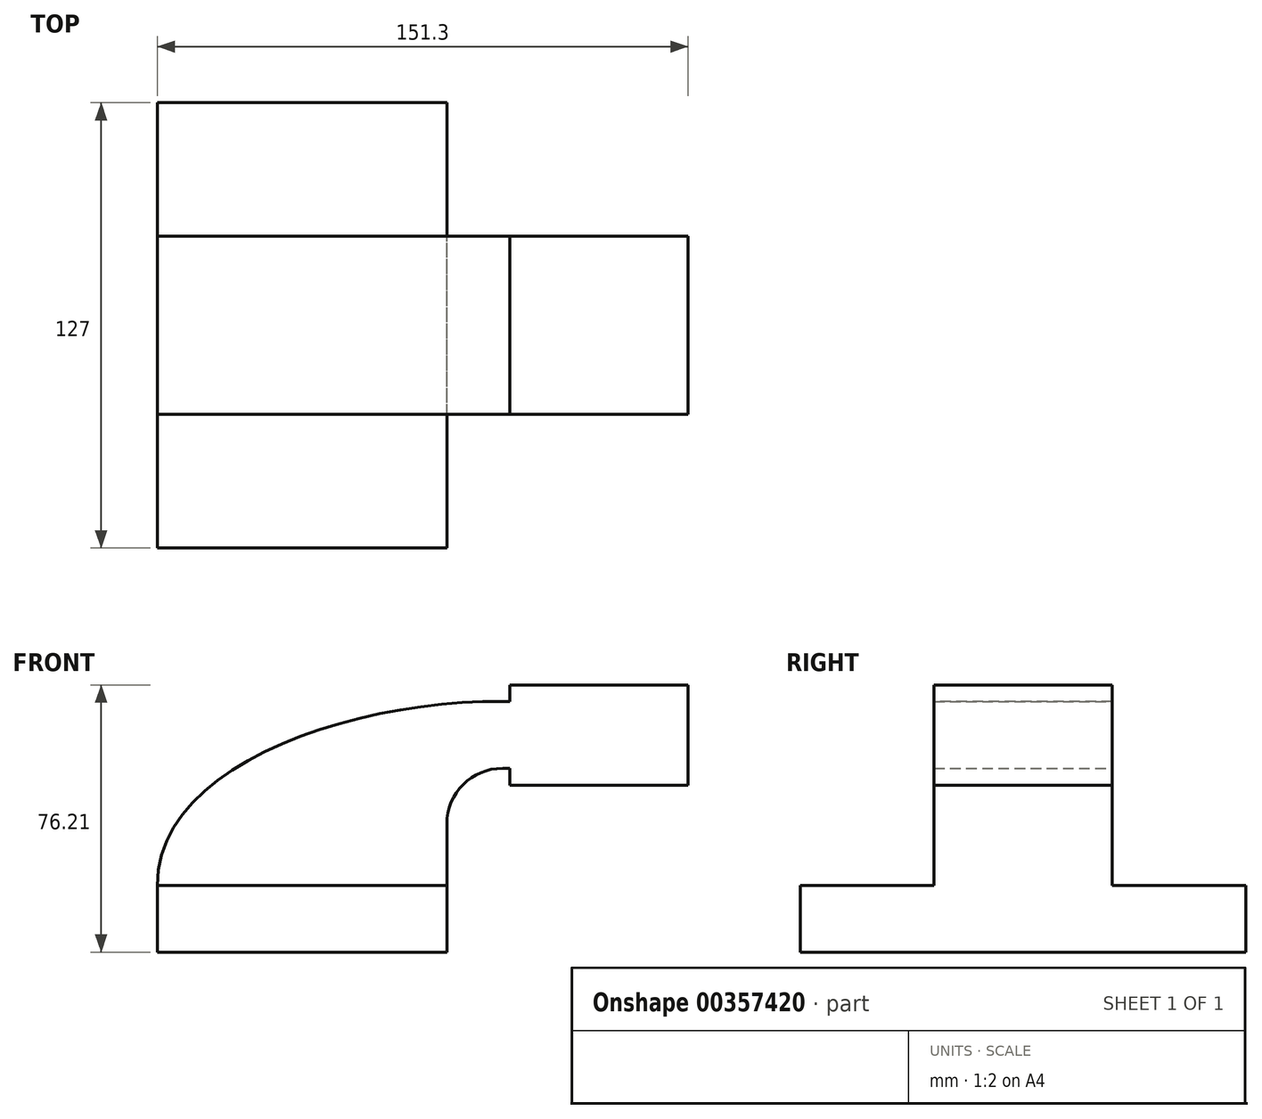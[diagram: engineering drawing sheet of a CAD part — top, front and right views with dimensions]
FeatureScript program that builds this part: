
annotation { "Feature Type Name" : "Feature", "Feature Type Description" : "" }
export const myFeature = defineFeature(function(context is Context, id is Id, definition is map)
    precondition{}
    {
        {
            var Q0;
            Q0=qCreatedBy(makeId("Front.planeOp"),FACE);
            var sketch = newSketch(context, id + "F0", { "sketchPlane" : qUnion([Q0])});
            skLineSegment(sketch, "E0.bottom", {"start": v(-41.28, -9.53) * mm, "end": v(41.28, -9.53) * mm});
            skLineSegment(sketch, "E0.top", {"start": v(-41.28, 9.53) * mm, "end": v(41.28, 9.53) * mm});
            skLineSegment(sketch, "E0.left", {"start": v(-41.27, -9.53) * mm, "end": v(-41.28, 9.53) * mm});
            skLineSegment(sketch, "E0.right", {"start": v(41.28, -9.53) * mm, "end": v(41.28, 9.53) * mm});
            skPoint(sketch, "E0.middle", {"position": v(0, 0) * mm});
            skLineSegment(sketch, "E1.bottom", {"start": v(59.22, 38.1) * mm, "end": v(110.02, 38.1) * mm});
            skLineSegment(sketch, "E1.top", {"start": v(59.22, 66.67) * mm, "end": v(110.02, 66.67) * mm});
            skLineSegment(sketch, "E1.left", {"start": v(59.22, 38.1) * mm, "end": v(59.22, 66.67) * mm});
            skLineSegment(sketch, "E1.right", {"start": v(110.02, 38.1) * mm, "end": v(110.02, 66.67) * mm});
            skPoint(sketch, "E1.middle", {"position": v(84.62, 52.39) * mm});
            skLineSegment(sketch, "E2", {"start": v(41.27, 9.53) * mm, "end": v(41.27, 27) * mm});
            skArc(sketch, "E3", {"start": v(41.27, 27) * mm, "mid": v(45.92, 38.23) * mm, "end": v(57.15, 42.88) * mm});
            skLineSegment(sketch, "E4", {"start": v(57.15, 42.88) * mm, "end": v(85.72, 42.88) * mm});
            skLineSegment(sketch, "E5.0", {"start": v(57.15, 61.93) * mm, "end": v(84.62, 61.93) * mm});
            skArc(sketch, "E5.1", {"start": v(22.22, 27) * mm, "mid": v(32.45, 51.7) * mm, "end": v(57.15, 61.93) * mm});
            skLineSegment(sketch, "E5.2", {"start": v(22.22, 9.53) * mm, "end": v(22.22, 27) * mm});
            skLineSegment(sketch, "E6", {"start": v(84.62, 38.1) * mm, "end": v(84.62, 66.68) * mm});
            skFitSpline(sketch, "E7", {"points": [v(-41.28, 9.53) * mm, v(57.15, 61.93) * mm], "startDerivative": vector(0.05, 102.9) * mm, "endDerivative": vector(129.47, -1.26) * mm});
            skSolve(sketch);
        }
        {
            var Q0;
            Q0=makeQuery(id+"F0.imprint","IMPRINT",FACE,{"disambiguationData":[TD([[makeQuery(id+"F0.imprint","IMPRINT",EDGE,{"derivedFrom":sQuery(id+"F0.wireOp",EDGE,"E0.bottom")}),1.0]])]});
            extrude(context, id + "F1", {"entities" : qUnion([Q0]), "endBound" : BoundingType.SYMMETRIC, "depth" : 127 * mm});
        }
        {
            var Q0;
            Q0 = qSketchRegion(id + "F0", true);
            extrude(context, id + "F2", {"entities" : qUnion([Q0]), "operationType" : NewBodyOperationType.ADD, "endBound" : BoundingType.SYMMETRIC, "depth" : 50.8 * mm});
        }
    });
